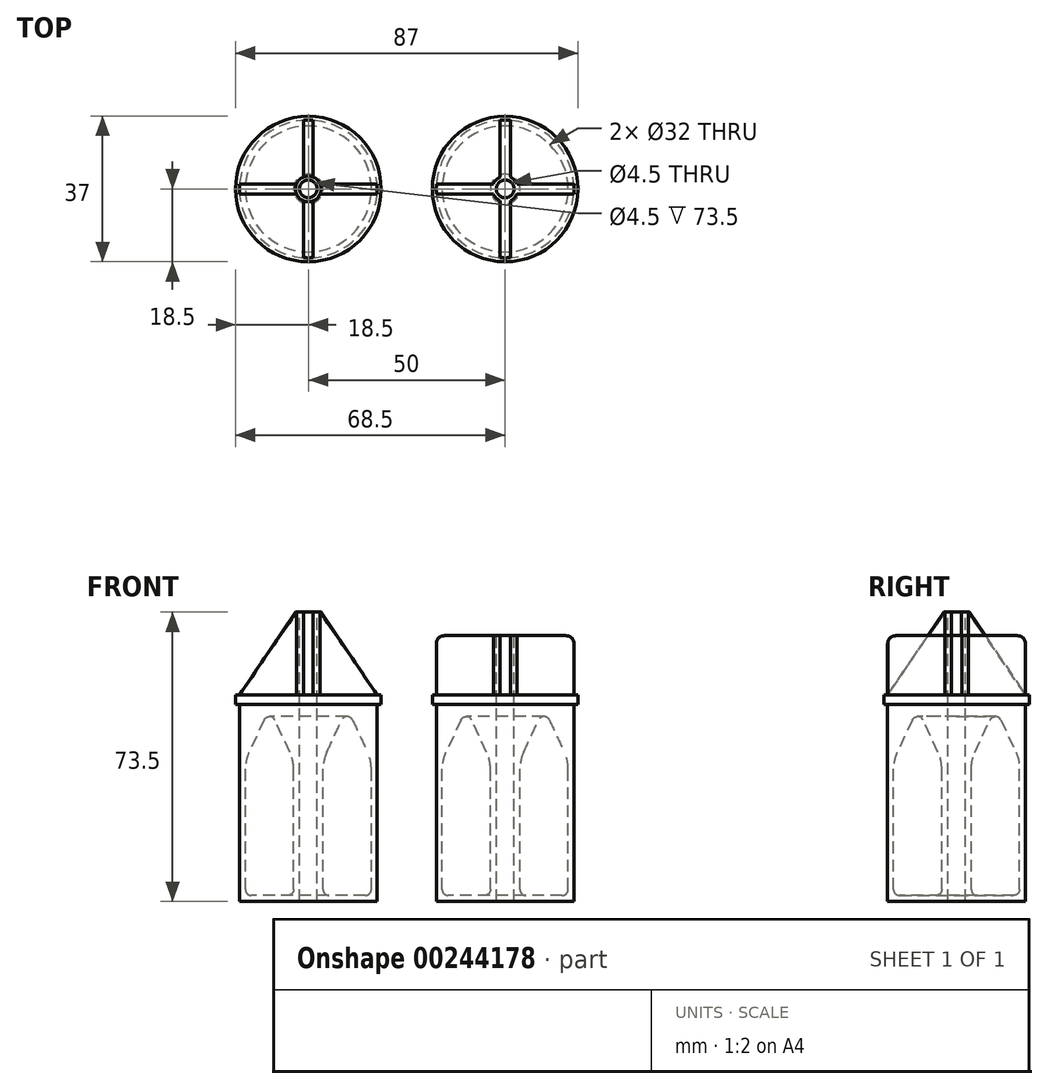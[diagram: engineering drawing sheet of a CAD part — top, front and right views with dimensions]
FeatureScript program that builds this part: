
annotation { "Feature Type Name" : "Feature", "Feature Type Description" : "" }
export const myFeature = defineFeature(function(context is Context, id is Id, definition is map)
    precondition{}
    {
        {
            assignVariable(context, id + "F0", {"name" : "scale", "anyValue" : 1});
        }
        {
            assignVariable(context, id + "F1", {"name" : "base_cylinder_height", "anyValue" : 50 * mm * getVariable(context, 'scale')});
        }
        {
            assignVariable(context, id + "F2", {"name" : "rim_height", "anyValue" : 2.5 * mm * getVariable(context, 'scale')});
        }
        {
            var Q0;
            Q0=qCreatedBy(makeId("Top.planeOp"),FACE);
            var sketch = newSketch(context, id + "F3", { "sketchPlane" : qUnion([Q0])});
            skCircle(sketch, "E0", {"center": v(0, 0) * mm, "radius": 17.5 * mm});
            skSolve(sketch);
        }
        {
            var Q0;
            Q0=makeQuery(id+"F3.imprint","IMPRINT",FACE,{"disambiguationData":[TD([[makeQuery(id+"F3.imprint","IMPRINT",EDGE,{"derivedFrom":sQuery(id+"F3.wireOp",EDGE,"E0")}),1.0]])]});
            extrude(context, id + "F4", {"entities" : qUnion([Q0]), "depth" : getVariable(context, 'base_cylinder_height')});
        }
        {
            var Q0;
            Q0=qCreatedBy(makeId("Front.planeOp"),FACE);
            var sketch = newSketch(context, id + "F5", { "sketchPlane" : qUnion([Q0])});
            skLineSegment(sketch, "E1.0", {"start": v(-17.5, 50) * mm, "end": v(17.5, 50) * mm, "construction": true});
            skLineSegment(sketch, "E1.1", {"start": v(-17.5, 0) * mm, "end": v(17.5, 0) * mm, "construction": true});
            skLineSegment(sketch, "E2", {"start": v(0, 0) * mm, "end": v(0, 50) * mm});
            skLineSegment(sketch, "E3", {"start": v(17.5, 0) * mm, "end": v(17.5, 50) * mm, "construction": true});
            skLineSegment(sketch, "E4", {"start": v(2.25, 0) * mm, "end": v(2.25, 50) * mm, "construction": true});
            skLineSegment(sketch, "E5.bottom", {"start": v(5.25, 1.5) * mm, "end": v(14.5, 1.5) * mm});
            skLineSegment(sketch, "E5.top", {"start": v(3.75, 35.86) * mm, "end": v(16, 35.86) * mm, "construction": true});
            skLineSegment(sketch, "E5.left", {"start": v(3.75, 3) * mm, "end": v(3.75, 33.65) * mm});
            skLineSegment(sketch, "E5.right", {"start": v(16, 3) * mm, "end": v(16, 33.65) * mm});
            skLineSegment(sketch, "E6", {"start": v(3.75, 35.86) * mm, "end": v(2.25, 35.86) * mm, "construction": true});
            skLineSegment(sketch, "E7", {"start": v(16, 35.86) * mm, "end": v(17.5, 35.86) * mm, "construction": true});
            skLineSegment(sketch, "E8", {"start": v(16, 1.5) * mm, "end": v(16, 0) * mm, "construction": true});
            skLineSegment(sketch, "E9", {"start": v(4.69, 37.87) * mm, "end": v(8.52, 46.08) * mm});
            skLineSegment(sketch, "E10", {"start": v(11.23, 46.08) * mm, "end": v(15.06, 37.87) * mm});
            skPoint(sketch, "E11.visualSharp", {"position": v(3.75, 35.86) * mm});
            skArc(sketch, "E11.filletArc", {"start": v(4.69, 37.87) * mm, "mid": v(3.99, 35.81) * mm, "end": v(3.75, 33.65) * mm});
            skPoint(sketch, "E12.visualSharp", {"position": v(16, 35.86) * mm});
            skArc(sketch, "E12.filletArc", {"start": v(16, 33.65) * mm, "mid": v(15.76, 35.81) * mm, "end": v(15.06, 37.87) * mm});
            skPoint(sketch, "E13.visualSharp", {"position": v(9.88, 49) * mm});
            skArc(sketch, "E13.filletArc", {"start": v(11.23, 46.08) * mm, "mid": v(9.87, 46.95) * mm, "end": v(8.52, 46.08) * mm});
            skPoint(sketch, "E14.visualSharp", {"position": v(3.75, 1.5) * mm});
            skArc(sketch, "E14.filletArc", {"start": v(3.75, 3) * mm, "mid": v(4.19, 1.94) * mm, "end": v(5.25, 1.5) * mm});
            skPoint(sketch, "E15.visualSharp", {"position": v(16, 1.5) * mm});
            skArc(sketch, "E15.filletArc", {"start": v(14.5, 1.5) * mm, "mid": v(15.56, 1.94) * mm, "end": v(16, 3) * mm});
            skSolve(sketch);
        }
        {
            var Q0;
            Q0=makeQuery(id+"F5.imprint","IMPRINT",FACE,{"disambiguationData":[TD([[makeQuery(id+"F5.imprint","IMPRINT",EDGE,{"derivedFrom":sQuery(id+"F5.wireOp",EDGE,"E5.bottom")}),1.0]])]});
            var Q1;
            Q1=sQuery(id+"F5.wireOp",EDGE,"E2");
            revolve(context, id + "F6", {"operationType" : NewBodyOperationType.REMOVE, "entities" : qUnion([Q0]), "axis" : qUnion([Q1]), "revolveType" : RevolveType.FULL, "oppositeDirection" : true});
        }
        {
            var Q0;
            Q0=makeQuery(id+"F4.opExtrude","CAP_FACE",FACE,{"disambiguationData":[OSD([sQuery(id+"F3.wireOp",EDGE,"E0")])],"isStart":false});
            var sketch = newSketch(context, id + "F7", { "sketchPlane" : qUnion([Q0])});
            skCircle(sketch, "E16", {"center": v(0, 0) * mm, "radius": 18.5 * mm});
            skSolve(sketch);
        }
        {
            var Q0;
            Q0=makeQuery(id+"F7.imprint","IMPRINT",FACE,{"disambiguationData":[TD([[makeQuery(id+"F7.imprint","IMPRINT",EDGE,{"derivedFrom":sQuery(id+"F7.wireOp",EDGE,"E16")}),1.0]])]});
            var Q1;
            Q1=makeQuery(id+"F7.imprint","IMPRINT",FACE,{"disambiguationData":[TD([[makeQuery(id+"F7.imprint","IMPRINT",EDGE,{"derivedFrom":makeQuery(id+"F4.opExtrude","CAP_EDGE",EDGE,{"disambiguationData":[OSD([sQuery(id+"F3.wireOp",EDGE,"E0")])],"isStart":false})}),1.0]])]});
            var Q2;
            Q2=sQuery(id+"F7.wireOp",EDGE,"E16");
            extrude(context, id + "F8", {"entities" : qUnion([Q0, Q1]), "operationType" : NewBodyOperationType.ADD, "surfaceEntities" : qUnion([Q2]), "depth" : getVariable(context, 'rim_height')});
        }
        {
            var Q0;
            Q0=makeQuery(id+"F4.opExtrude","SWEPT_BODY",BODY,{"disambiguationData":[OSD([sQuery(id+"F3.wireOp",EDGE,"E0")])]});
            transform(context, id + "F9", {"entities" : qUnion([Q0]), "transformType" : TransformType.TRANSLATION_3D, "dx" : 50 * mm * getVariable(context, 'scale'), "dy" : 0 * mm, "dz" : 0 * mm, "makeCopy" : true});
        }
        {
            var Q0;
            Q0=qCreatedBy(makeId("Front.planeOp"),FACE);
            var sketch = newSketch(context, id + "F10", { "sketchPlane" : qUnion([Q0])});
            skLineSegment(sketch, "E17.0", {"start": v(-17.5, 50) * mm, "end": v(17.5, 50) * mm, "construction": true});
            skLineSegment(sketch, "E18.0", {"start": v(-18.5, 52.5) * mm, "end": v(-17.5, 52.5) * mm, "construction": true});
            skLineSegment(sketch, "E19", {"start": v(-17.5, 50) * mm, "end": v(-17.5, 52.5) * mm, "construction": true});
            skLineSegment(sketch, "E20", {"start": v(0, 50) * mm, "end": v(0, 52.5) * mm, "construction": true});
            skLineSegment(sketch, "E21", {"start": v(-17.5, 52.5) * mm, "end": v(0, 52.5) * mm});
            skLineSegment(sketch, "E22", {"start": v(0, 52.5) * mm, "end": v(18.5, 52.5) * mm, "construction": true});
            skLineSegment(sketch, "E23", {"start": v(0, 52.5) * mm, "end": v(0, 73.5) * mm});
            skLineSegment(sketch, "E24", {"start": v(0, 73.5) * mm, "end": v(-3.25, 73.5) * mm});
            skLineSegment(sketch, "E25", {"start": v(-3.25, 73.5) * mm, "end": v(-17.5, 52.5) * mm});
            skSolve(sketch);
        }
        {
            var Q0;
            Q0=makeQuery(id+"F10.imprint","IMPRINT",FACE,{"disambiguationData":[TD([[makeQuery(id+"F10.imprint","IMPRINT",EDGE,{"derivedFrom":sQuery(id+"F10.wireOp",EDGE,"E21")}),1.0]])]});
            var Q1;
            Q1=sQuery(id+"F10.wireOp",EDGE,"E23");
            revolve(context, id + "F11", {"operationType" : NewBodyOperationType.ADD, "entities" : qUnion([Q0]), "axis" : qUnion([Q1]), "revolveType" : RevolveType.FULL});
        }
        {
            var Q0;
            Q0=makeQuery(id+"F11.opRevolve","SWEPT_FACE",FACE,{"disambiguationData":[OSD([sQuery(id+"F10.wireOp",EDGE,"E24")])]});
            var sketch = newSketch(context, id + "F12", { "sketchPlane" : qUnion([Q0])});
            skLineSegment(sketch, "E26", {"start": v(-17.46, 1.25) * mm, "end": v(-3, 1.25) * mm});
            skLineSegment(sketch, "E27", {"start": v(-17.46, -1.25) * mm, "end": v(-3, -1.25) * mm});
            skLineSegment(sketch, "E28", {"start": v(-1.25, -3) * mm, "end": v(-1.25, -17.46) * mm});
            skLineSegment(sketch, "E29", {"start": v(1.25, -3) * mm, "end": v(1.25, -17.46) * mm});
            skLineSegment(sketch, "E30", {"start": v(3, -1.25) * mm, "end": v(17.46, -1.25) * mm});
            skLineSegment(sketch, "E31", {"start": v(3, 1.25) * mm, "end": v(17.46, 1.25) * mm});
            skLineSegment(sketch, "E32", {"start": v(1.25, 3) * mm, "end": v(1.25, 17.46) * mm});
            skLineSegment(sketch, "E33", {"start": v(-1.25, 3) * mm, "end": v(-1.25, 17.46) * mm});
            skLineSegment(sketch, "E34", {"start": v(-1.25, 12.14) * mm, "end": v(0, 12.14) * mm, "construction": true});
            skLineSegment(sketch, "E35", {"start": v(0, 12.14) * mm, "end": v(1.25, 12.14) * mm, "construction": true});
            skLineSegment(sketch, "E36", {"start": v(-13.64, 1.25) * mm, "end": v(-13.64, 0) * mm, "construction": true});
            skLineSegment(sketch, "E37", {"start": v(-13.64, 0) * mm, "end": v(-13.64, -1.25) * mm, "construction": true});
            skArc(sketch, "E38", {"start": v(-17.46, 1.25) * mm, "mid": v(-12.37, 12.37) * mm, "end": v(-1.25, 17.46) * mm});
            skArc(sketch, "E39", {"start": v(-1.25, 17.46) * mm, "mid": v(0, 17.5) * mm, "end": v(1.25, 17.46) * mm, "construction": true});
            skArc(sketch, "E40", {"start": v(-17.46, -1.25) * mm, "mid": v(-17.5, 0) * mm, "end": v(-17.46, 1.25) * mm, "construction": true});
            skArc(sketch, "E41", {"start": v(-1.25, -17.46) * mm, "mid": v(-12.37, -12.37) * mm, "end": v(-17.46, -1.25) * mm});
            skArc(sketch, "E42", {"start": v(1.25, -17.46) * mm, "mid": v(0, -17.5) * mm, "end": v(-1.25, -17.46) * mm, "construction": true});
            skArc(sketch, "E43", {"start": v(17.46, -1.25) * mm, "mid": v(12.37, -12.37) * mm, "end": v(1.25, -17.46) * mm});
            skArc(sketch, "E44", {"start": v(17.46, 1.25) * mm, "mid": v(17.5, 0) * mm, "end": v(17.46, -1.25) * mm, "construction": true});
            skArc(sketch, "E45", {"start": v(1.25, 17.46) * mm, "mid": v(12.37, 12.37) * mm, "end": v(17.46, 1.25) * mm});
            skArc(sketch, "E46", {"start": v(-3, 1.25) * mm, "mid": v(-2.3, 2.3) * mm, "end": v(-1.25, 3) * mm});
            skArc(sketch, "E47", {"start": v(-1.25, 3) * mm, "mid": v(0, 3.25) * mm, "end": v(1.25, 3) * mm, "construction": true});
            skArc(sketch, "E48", {"start": v(1.25, 3) * mm, "mid": v(2.3, 2.3) * mm, "end": v(3, 1.25) * mm});
            skArc(sketch, "E49", {"start": v(3, 1.25) * mm, "mid": v(3.25, 0) * mm, "end": v(3, -1.25) * mm, "construction": true});
            skArc(sketch, "E50", {"start": v(3, -1.25) * mm, "mid": v(2.3, -2.3) * mm, "end": v(1.25, -3) * mm});
            skArc(sketch, "E51", {"start": v(1.25, -3) * mm, "mid": v(0, -3.25) * mm, "end": v(-1.25, -3) * mm, "construction": true});
            skArc(sketch, "E52", {"start": v(-1.25, -3) * mm, "mid": v(-2.3, -2.3) * mm, "end": v(-3, -1.25) * mm});
            skArc(sketch, "E53", {"start": v(-3, -1.25) * mm, "mid": v(-3.25, 0) * mm, "end": v(-3, 1.25) * mm, "construction": true});
            skSolve(sketch);
        }
        {
            var Q0;
            Q0=makeQuery(id+"F12.imprint","IMPRINT",FACE,{"disambiguationData":[TD([[makeQuery(id+"F12.imprint","IMPRINT",EDGE,{"derivedFrom":sQuery(id+"F12.wireOp",EDGE,"E26")}),1.0]])]});
            var Q1;
            Q1=makeQuery(id+"F12.imprint","IMPRINT",FACE,{"disambiguationData":[TD([[makeQuery(id+"F12.imprint","IMPRINT",EDGE,{"derivedFrom":sQuery(id+"F12.wireOp",EDGE,"E31")}),1.0]])]});
            var Q2;
            Q2=makeQuery(id+"F12.imprint","IMPRINT",FACE,{"disambiguationData":[TD([[makeQuery(id+"F12.imprint","IMPRINT",EDGE,{"derivedFrom":sQuery(id+"F12.wireOp",EDGE,"E29")}),1.0]])]});
            var Q3;
            Q3=makeQuery(id+"F12.imprint","IMPRINT",FACE,{"disambiguationData":[TD([[makeQuery(id+"F12.imprint","IMPRINT",EDGE,{"derivedFrom":sQuery(id+"F12.wireOp",EDGE,"E27")}),-1.0]])]});
            var Q4;
            Q4=makeQuery(id+"F8.opExtrude","CAP_FACE",FACE,{"disambiguationData":[OSD([sQuery(id+"F7.wireOp",EDGE,"E16")])],"isStart":false});
            extrude(context, id + "F13", {"entities" : qUnion([Q0, Q1, Q2, Q3]), "operationType" : NewBodyOperationType.REMOVE, "endBound" : BoundingType.UP_TO_SURFACE, "oppositeDirection" : true, "endBoundEntityFace" : qUnion([Q4]), "depth" : 25 * mm});
        }
        {
            var Q0;
            Q0=makeQuery(id+"F11.opRevolve","SWEPT_FACE",FACE,{"disambiguationData":[OSD([sQuery(id+"F10.wireOp",EDGE,"E24")])]});
            var sketch = newSketch(context, id + "F14", { "sketchPlane" : qUnion([Q0])});
            skCircle(sketch, "E54", {"center": v(0, 0) * mm, "radius": 2.25 * mm});
            skSolve(sketch);
        }
        {
            var Q0;
            Q0 = qSketchRegion(id + "F14", true);
            var Q1;
            Q1=makeQuery(id+"F4.opExtrude","CAP_FACE",FACE,{"disambiguationData":[OSD([sQuery(id+"F3.wireOp",EDGE,"E0")])],"isStart":true});
            extrude(context, id + "F15", {"entities" : qUnion([Q0]), "operationType" : NewBodyOperationType.REMOVE, "endBound" : BoundingType.UP_TO_SURFACE, "oppositeDirection" : true, "endBoundEntityFace" : qUnion([Q1]), "depth" : 25 * mm});
        }
        {
            var Q0;
            Q0=qCreatedBy(makeId("Front.planeOp"),FACE);
            var sketch = newSketch(context, id + "F16", { "sketchPlane" : qUnion([Q0])});
            skLineSegment(sketch, "E55.0", {"start": v(32.5, 50) * mm, "end": v(67.5, 50) * mm, "construction": true});
            skLineSegment(sketch, "E56.0", {"start": v(31.5, 52.5) * mm, "end": v(32.5, 52.5) * mm, "construction": true});
            skLineSegment(sketch, "E57", {"start": v(50, 50) * mm, "end": v(50, 52.5) * mm, "construction": true});
            skLineSegment(sketch, "E58", {"start": v(32.5, 50) * mm, "end": v(32.5, 52.5) * mm, "construction": true});
            skLineSegment(sketch, "E59", {"start": v(32.5, 52.5) * mm, "end": v(50, 52.5) * mm});
            skLineSegment(sketch, "E60", {"start": v(50, 52.5) * mm, "end": v(68.5, 52.5) * mm, "construction": true});
            skLineSegment(sketch, "E61", {"start": v(50, 52.5) * mm, "end": v(50, 67.5) * mm});
            skLineSegment(sketch, "E62", {"start": v(50, 67.5) * mm, "end": v(34.5, 67.5) * mm});
            skLineSegment(sketch, "E63", {"start": v(32.5, 52.5) * mm, "end": v(32.5, 65.5) * mm});
            skPoint(sketch, "E64.visualSharp", {"position": v(32.5, 67.5) * mm});
            skArc(sketch, "E64.filletArc", {"start": v(34.5, 67.5) * mm, "mid": v(33.09, 66.91) * mm, "end": v(32.5, 65.5) * mm});
            skSolve(sketch);
        }
        {
            var Q0;
            Q0=makeQuery(id+"F16.imprint","IMPRINT",FACE,{"disambiguationData":[TD([[makeQuery(id+"F16.imprint","IMPRINT",EDGE,{"derivedFrom":sQuery(id+"F16.wireOp",EDGE,"E59")}),1.0]])]});
            var Q1;
            Q1=sQuery(id+"F16.wireOp",EDGE,"E61");
            revolve(context, id + "F17", {"operationType" : NewBodyOperationType.ADD, "entities" : qUnion([Q0]), "axis" : qUnion([Q1]), "revolveType" : RevolveType.FULL});
        }
        {
            var Q0;
            Q0=makeQuery(id+"F17.opRevolve","SWEPT_FACE",FACE,{"disambiguationData":[OSD([sQuery(id+"F16.wireOp",EDGE,"E62")])]});
            var sketch = newSketch(context, id + "F18", { "sketchPlane" : qUnion([Q0])});
            skLineSegment(sketch, "E65", {"start": v(48.7, 17.45) * mm, "end": v(48.7, 2.98) * mm});
            skLineSegment(sketch, "E66", {"start": v(51.3, 17.45) * mm, "end": v(51.3, 2.98) * mm});
            skLineSegment(sketch, "E67", {"start": v(51.3, -2.98) * mm, "end": v(51.3, -17.45) * mm});
            skLineSegment(sketch, "E68", {"start": v(48.7, -2.98) * mm, "end": v(48.7, -17.45) * mm});
            skLineSegment(sketch, "E69", {"start": v(52.98, -1.3) * mm, "end": v(67.45, -1.3) * mm});
            skLineSegment(sketch, "E70", {"start": v(52.98, 1.3) * mm, "end": v(67.45, 1.3) * mm});
            skLineSegment(sketch, "E71", {"start": v(47.02, 1.3) * mm, "end": v(32.55, 1.3) * mm});
            skLineSegment(sketch, "E72", {"start": v(47.02, -1.3) * mm, "end": v(32.55, -1.3) * mm});
            skLineSegment(sketch, "E73", {"start": v(50, 0) * mm, "end": v(50, 17.5) * mm, "construction": true});
            skLineSegment(sketch, "E74", {"start": v(48.7, 14.44) * mm, "end": v(50, 14.44) * mm, "construction": true});
            skLineSegment(sketch, "E75", {"start": v(50, 14.44) * mm, "end": v(51.3, 14.44) * mm, "construction": true});
            skLineSegment(sketch, "E76", {"start": v(50, 0) * mm, "end": v(32.5, 0) * mm, "construction": true});
            skLineSegment(sketch, "E77", {"start": v(35.38, 1.3) * mm, "end": v(35.38, 0) * mm, "construction": true});
            skLineSegment(sketch, "E78", {"start": v(35.38, 0) * mm, "end": v(35.38, -1.3) * mm, "construction": true});
            skArc(sketch, "E79", {"start": v(48.7, 17.45) * mm, "mid": v(37.63, 12.37) * mm, "end": v(32.55, 1.3) * mm});
            skArc(sketch, "E80", {"start": v(32.55, 1.3) * mm, "mid": v(32.5, 0) * mm, "end": v(32.55, -1.3) * mm, "construction": true});
            skArc(sketch, "E81", {"start": v(32.55, -1.3) * mm, "mid": v(37.63, -12.37) * mm, "end": v(48.7, -17.45) * mm});
            skArc(sketch, "E82", {"start": v(51.3, 17.45) * mm, "mid": v(50, 17.5) * mm, "end": v(48.7, 17.45) * mm, "construction": true});
            skArc(sketch, "E83", {"start": v(67.45, 1.3) * mm, "mid": v(62.37, 12.37) * mm, "end": v(51.3, 17.45) * mm});
            skArc(sketch, "E84", {"start": v(67.45, -1.3) * mm, "mid": v(67.5, 0) * mm, "end": v(67.45, 1.3) * mm, "construction": true});
            skArc(sketch, "E85", {"start": v(51.3, -17.45) * mm, "mid": v(62.37, -12.37) * mm, "end": v(67.45, -1.3) * mm});
            skArc(sketch, "E86", {"start": v(48.7, -17.45) * mm, "mid": v(50, -17.5) * mm, "end": v(51.3, -17.45) * mm, "construction": true});
            skArc(sketch, "E87", {"start": v(48.7, 2.98) * mm, "mid": v(47.7, 2.3) * mm, "end": v(47.02, 1.3) * mm});
            skArc(sketch, "E88", {"start": v(47.02, 1.3) * mm, "mid": v(46.75, 0) * mm, "end": v(47.02, -1.3) * mm, "construction": true});
            skArc(sketch, "E89", {"start": v(51.3, 2.98) * mm, "mid": v(50, 3.25) * mm, "end": v(48.7, 2.98) * mm, "construction": true});
            skArc(sketch, "E90", {"start": v(52.98, 1.3) * mm, "mid": v(52.3, 2.3) * mm, "end": v(51.3, 2.98) * mm});
            skArc(sketch, "E91", {"start": v(52.98, -1.3) * mm, "mid": v(53.25, 0) * mm, "end": v(52.98, 1.3) * mm, "construction": true});
            skArc(sketch, "E92", {"start": v(51.3, -2.98) * mm, "mid": v(52.3, -2.3) * mm, "end": v(52.98, -1.3) * mm});
            skArc(sketch, "E93", {"start": v(48.7, -2.98) * mm, "mid": v(50, -3.25) * mm, "end": v(51.3, -2.98) * mm, "construction": true});
            skArc(sketch, "E94", {"start": v(47.02, -1.3) * mm, "mid": v(47.7, -2.3) * mm, "end": v(48.7, -2.98) * mm});
            skSolve(sketch);
        }
        {
            var Q0;
            Q0 = qSketchRegion(id + "F18", true);
            var Q1;
            Q1=makeQuery(id+"F9.opPattern","COPY",FACE,{"derivedFrom":makeQuery(id+"F8.opExtrude","CAP_FACE",FACE,{"disambiguationData":[OSD([sQuery(id+"F7.wireOp",EDGE,"E16")])],"isStart":false}),"instanceName":"1"});
            extrude(context, id + "F19", {"entities" : qUnion([Q0]), "operationType" : NewBodyOperationType.REMOVE, "endBound" : BoundingType.UP_TO_SURFACE, "oppositeDirection" : true, "endBoundEntityFace" : qUnion([Q1]), "depth" : 25 * mm});
        }
        {
            var Q0;
            Q0=makeQuery(id+"F17.opRevolve","SWEPT_FACE",FACE,{"disambiguationData":[OSD([sQuery(id+"F16.wireOp",EDGE,"E62")])]});
            var sketch = newSketch(context, id + "F20", { "sketchPlane" : qUnion([Q0])});
            skCircle(sketch, "E95", {"center": v(50, 0) * mm, "radius": 2.25 * mm});
            skSolve(sketch);
        }
        {
            var Q0;
            Q0=makeQuery(id+"F20.imprint","IMPRINT",FACE,{"disambiguationData":[TD([[makeQuery(id+"F20.imprint","IMPRINT",EDGE,{"derivedFrom":sQuery(id+"F20.wireOp",EDGE,"E95")}),1.0]])]});
            var Q1;
            Q1=makeQuery(id+"F9.opPattern","COPY",FACE,{"derivedFrom":makeQuery(id+"F4.opExtrude","CAP_FACE",FACE,{"disambiguationData":[OSD([sQuery(id+"F3.wireOp",EDGE,"E0")])],"isStart":true}),"instanceName":"1"});
            extrude(context, id + "F21", {"entities" : qUnion([Q0]), "operationType" : NewBodyOperationType.REMOVE, "endBound" : BoundingType.UP_TO_SURFACE, "oppositeDirection" : true, "endBoundEntityFace" : qUnion([Q1]), "depth" : 25 * mm});
        }
    });
